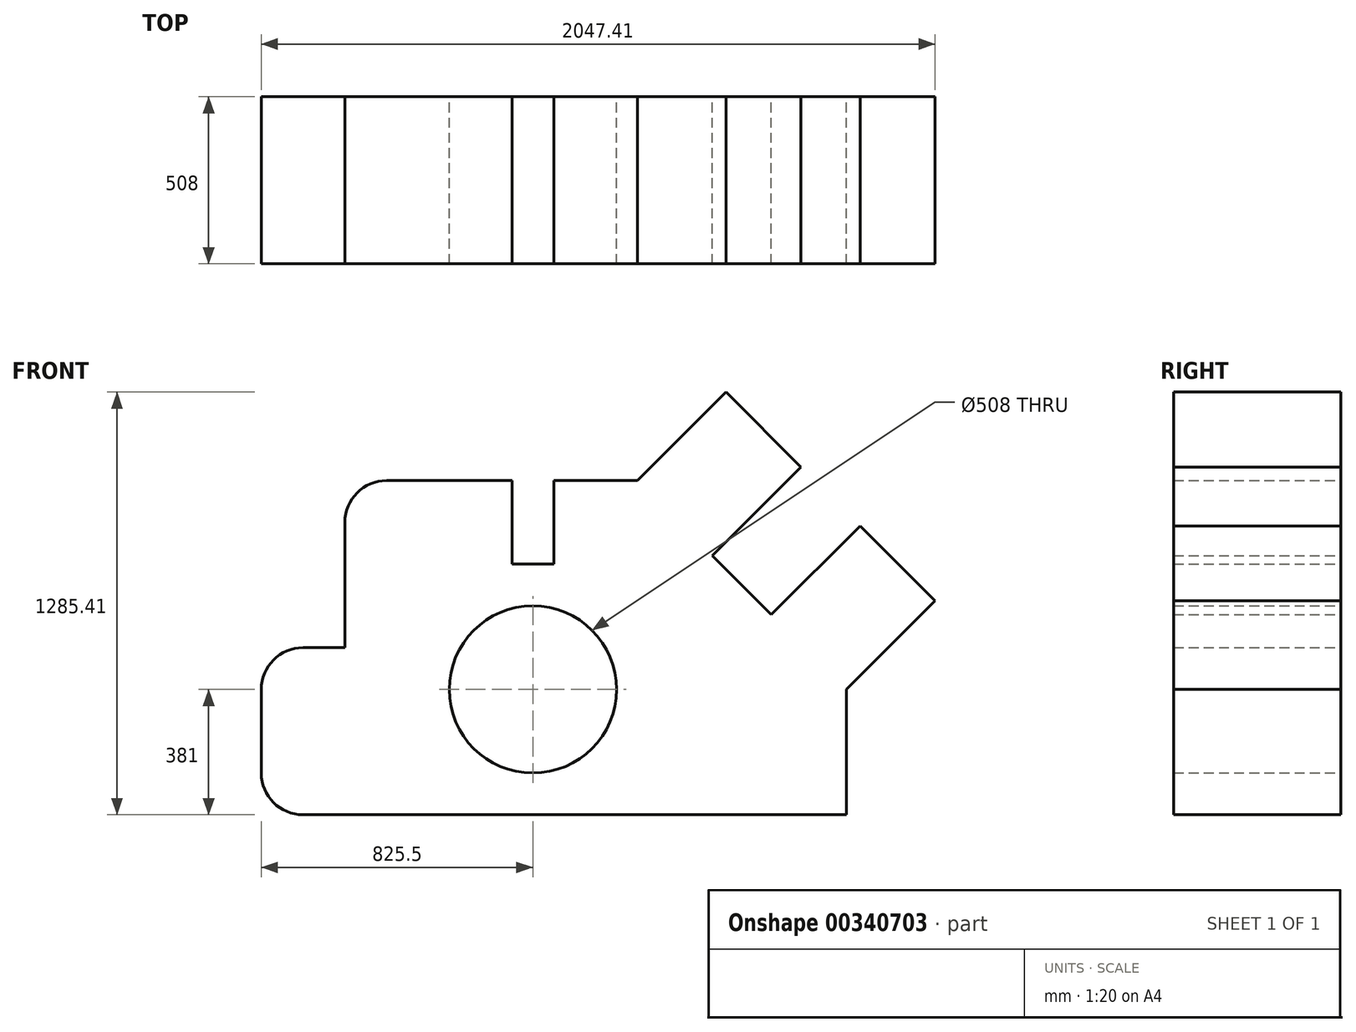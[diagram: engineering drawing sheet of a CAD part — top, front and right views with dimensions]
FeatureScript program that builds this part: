
annotation { "Feature Type Name" : "Feature", "Feature Type Description" : "" }
export const myFeature = defineFeature(function(context is Context, id is Id, definition is map)
    precondition{}
    {
        {
            var Q0;
            Q0=qCreatedBy(makeId("Front.planeOp"),FACE);
            var sketch = newSketch(context, id + "F0", { "sketchPlane" : qUnion([Q0])});
            skLineSegment(sketch, "E0", {"start": v(0, 0) * mm, "end": v(1778, 0) * mm});
            skLineSegment(sketch, "E1", {"start": v(1778, 0) * mm, "end": v(1778, 381) * mm});
            skLineSegment(sketch, "E2", {"start": v(1778, 381) * mm, "end": v(2047.4, 650.4) * mm});
            skLineSegment(sketch, "E3", {"start": v(2047.4, 650.4) * mm, "end": v(1819.71, 878.1) * mm});
            skLineSegment(sketch, "E4", {"start": v(1819.71, 878.1) * mm, "end": v(1550.3, 608.7) * mm});
            skLineSegment(sketch, "E5", {"start": v(1550.3, 608.7) * mm, "end": v(1370.7, 788.3) * mm});
            skLineSegment(sketch, "E6", {"start": v(1370.7, 788.3) * mm, "end": v(1640.1, 1057.71) * mm});
            skLineSegment(sketch, "E7", {"start": v(1640.1, 1057.71) * mm, "end": v(1412.4, 1285.4) * mm});
            skLineSegment(sketch, "E8", {"start": v(1412.4, 1285.4) * mm, "end": v(1143, 1016) * mm});
            skLineSegment(sketch, "E9", {"start": v(1143, 1016) * mm, "end": v(889, 1016) * mm});
            skLineSegment(sketch, "E10", {"start": v(889, 1016) * mm, "end": v(889, 762) * mm});
            skLineSegment(sketch, "E11", {"start": v(889, 762) * mm, "end": v(762, 762) * mm});
            skLineSegment(sketch, "E12", {"start": v(762, 762) * mm, "end": v(762, 1016) * mm});
            skLineSegment(sketch, "E13", {"start": v(762, 1016) * mm, "end": v(254, 1016) * mm});
            skLineSegment(sketch, "E14", {"start": v(254, 1016) * mm, "end": v(254, 508) * mm});
            skLineSegment(sketch, "E15", {"start": v(254, 508) * mm, "end": v(0, 508) * mm});
            skLineSegment(sketch, "E16", {"start": v(0, 508) * mm, "end": v(0, 0) * mm});
            skCircle(sketch, "E17", {"center": v(825.5, 381) * mm, "radius": 254 * mm});
            skSolve(sketch);
        }
        {
            var Q0;
            Q0=makeQuery(id+"F0.imprint","IMPRINT",FACE,{"disambiguationData":[TD([[makeQuery(id+"F0.imprint","IMPRINT",EDGE,{"derivedFrom":sQuery(id+"F0.wireOp",EDGE,"E0")}),1.0]])]});
            extrude(context, id + "F1", {"entities" : qUnion([Q0]), "depth" : 508 * mm});
        }
        {
            var Q0;
            Q0=makeQuery(id+"F1.opExtrude","SWEPT_EDGE",EDGE,{"disambiguationData":[OSD([sQuery(id+"F0.wireOp",EDGE,"E13"),sQuery(id+"F0.wireOp",EDGE,"E14")])]});
            var Q1;
            Q1=makeQuery(id+"F1.opExtrude","SWEPT_EDGE",EDGE,{"disambiguationData":[OSD([sQuery(id+"F0.wireOp",EDGE,"E15"),sQuery(id+"F0.wireOp",EDGE,"E16")])]});
            var Q2;
            Q2=makeQuery(id+"F1.opExtrude","SWEPT_EDGE",EDGE,{"disambiguationData":[OSD([sQuery(id+"F0.wireOp",EDGE,"E0"),sQuery(id+"F0.wireOp",EDGE,"E16")])]});
            fillet(context, id + "F2", {"entities" : qUnion([Q0, Q1, Q2]), "radius" : 127 * mm, "tangentPropagation" : true, "allowEdgeOverflow" : false});
        }
    });
